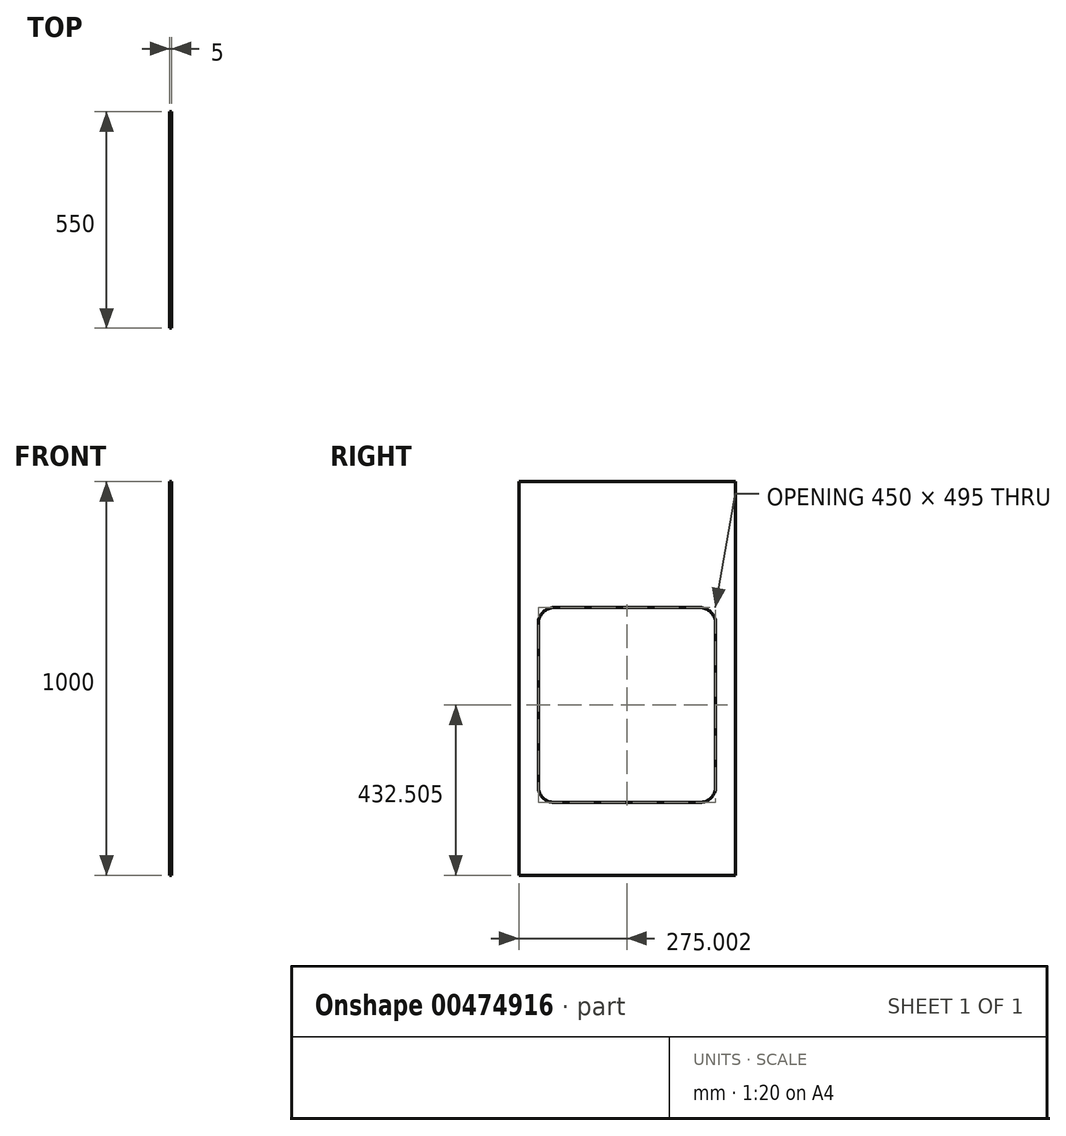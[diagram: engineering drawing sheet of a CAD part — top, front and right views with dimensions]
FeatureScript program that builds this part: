
annotation { "Feature Type Name" : "Feature", "Feature Type Description" : "" }
export const myFeature = defineFeature(function(context is Context, id is Id, definition is map)
    precondition{}
    {
        {
            var Q0;
            Q0=qCreatedBy(makeId("Right.planeOp"),FACE);
            var sketch = newSketch(context, id + "F0", { "sketchPlane" : qUnion([Q0])});
            skLineSegment(sketch, "E0.bottom", {"start": v(-279.26, 365.08) * mm, "end": v(270.74, 365.08) * mm});
            skLineSegment(sketch, "E0.top", {"start": v(-279.26, -229.92) * mm, "end": v(270.74, -229.92) * mm});
            skLineSegment(sketch, "E0.left", {"start": v(-279.26, 365.08) * mm, "end": v(-279.26, -229.92) * mm});
            skLineSegment(sketch, "E0.right", {"start": v(270.74, 365.08) * mm, "end": v(270.74, -229.92) * mm});
            skLineSegment(sketch, "E1.bottom", {"start": v(-189.26, 315.08) * mm, "end": v(-4.26, 315.08) * mm});
            skLineSegment(sketch, "E1.left", {"start": v(-229.26, 275.08) * mm, "end": v(-229.26, 67.58) * mm});
            skArc(sketch, "E2", {"start": v(-189.26, 315.08) * mm, "mid": v(-217.54, 303.37) * mm, "end": v(-229.26, 275.08) * mm});
            skPoint(sketch, "E3.orphan", {"position": v(-229.26, 315.08) * mm});
            skPoint(sketch, "E4", {"position": v(-4.26, -179.92) * mm});
            skLineSegment(sketch, "E5", {"start": v(-4.26, -179.92) * mm, "end": v(-4.26, 315.08) * mm, "construction": true});
            skPoint(sketch, "E5.endSnap0", {"position": v(-4.26, 365.08) * mm});
            skPoint(sketch, "E6", {"position": v(-4.26, 67.58) * mm});
            skLineSegment(sketch, "E7", {"start": v(-4.26, 67.58) * mm, "end": v(-229.26, 67.58) * mm, "construction": true});
            skLineSegment(sketch, "E8.MirrorCS", {"start": v(180.74, 315.08) * mm, "end": v(-4.26, 315.08) * mm});
            skArc(sketch, "E9.MirrorCS", {"start": v(180.74, 315.08) * mm, "mid": v(209.03, 303.37) * mm, "end": v(220.74, 275.08) * mm});
            skLineSegment(sketch, "E10.MirrorCS", {"start": v(220.74, 275.08) * mm, "end": v(220.74, 67.58) * mm});
            skArc(sketch, "E11.MirrorCS", {"start": v(180.74, -179.92) * mm, "mid": v(209.03, -168.2) * mm, "end": v(220.74, -139.92) * mm});
            skArc(sketch, "E12.MirrorCS", {"start": v(-189.26, -179.92) * mm, "mid": v(-217.54, -168.2) * mm, "end": v(-229.26, -139.92) * mm});
            skLineSegment(sketch, "E13.MirrorCS", {"start": v(180.74, -179.92) * mm, "end": v(-4.26, -179.92) * mm});
            skLineSegment(sketch, "E14.MirrorCS", {"start": v(220.74, -139.92) * mm, "end": v(220.74, 67.58) * mm});
            skLineSegment(sketch, "E15.MirrorCS", {"start": v(-4.26, 315.08) * mm, "end": v(-4.26, -179.92) * mm, "construction": true});
            skLineSegment(sketch, "E16.MirrorCS", {"start": v(-229.26, -139.92) * mm, "end": v(-229.26, 67.58) * mm});
            skLineSegment(sketch, "E17.MirrorCS", {"start": v(-189.26, -179.92) * mm, "end": v(-4.26, -179.92) * mm});
            skLineSegment(sketch, "E18", {"start": v(-279.26, -229.92) * mm, "end": v(-279.26, -364.92) * mm});
            skLineSegment(sketch, "E19", {"start": v(270.74, -364.92) * mm, "end": v(-279.26, -364.92) * mm});
            skLineSegment(sketch, "E20", {"start": v(270.74, -364.92) * mm, "end": v(270.74, -229.92) * mm});
            skLineSegment(sketch, "E21", {"start": v(-279.26, 365.08) * mm, "end": v(-279.26, 635.08) * mm});
            skLineSegment(sketch, "E22", {"start": v(-279.26, 635.08) * mm, "end": v(270.74, 635.08) * mm});
            skLineSegment(sketch, "E23", {"start": v(270.74, 635.08) * mm, "end": v(270.74, 365.08) * mm});
            skSolve(sketch);
        }
        {
            var Q0;
            Q0=makeQuery(id+"F0.imprint","IMPRINT",FACE,{"disambiguationData":[TD([[makeQuery(id+"F0.imprint","IMPRINT",EDGE,{"derivedFrom":sQuery(id+"F0.wireOp",EDGE,"E0.bottom")}),-1.0]])]});
            extrude(context, id + "F1", {"entities" : qUnion([Q0]), "depth" : 5 * mm, "offsetDistance" : 25 * mm});
        }
        {
            var Q0;
            Q0=makeQuery(id+"F0.imprint","IMPRINT",FACE,{"disambiguationData":[TD([[makeQuery(id+"F0.imprint","IMPRINT",EDGE,{"derivedFrom":sQuery(id+"F0.wireOp",EDGE,"E0.bottom")}),1.0]])]});
            extrude(context, id + "F2", {"entities" : qUnion([Q0]), "operationType" : NewBodyOperationType.ADD, "depth" : 5 * mm, "offsetDistance" : 25 * mm});
        }
        {
            var Q0;
            Q0=makeQuery(id+"F0.imprint","IMPRINT",FACE,{"disambiguationData":[TD([[makeQuery(id+"F0.imprint","IMPRINT",EDGE,{"derivedFrom":sQuery(id+"F0.wireOp",EDGE,"E0.top")}),-1.0]])]});
            extrude(context, id + "F3", {"entities" : qUnion([Q0]), "operationType" : NewBodyOperationType.ADD, "depth" : 5 * mm, "offsetDistance" : 25 * mm});
        }
    });
